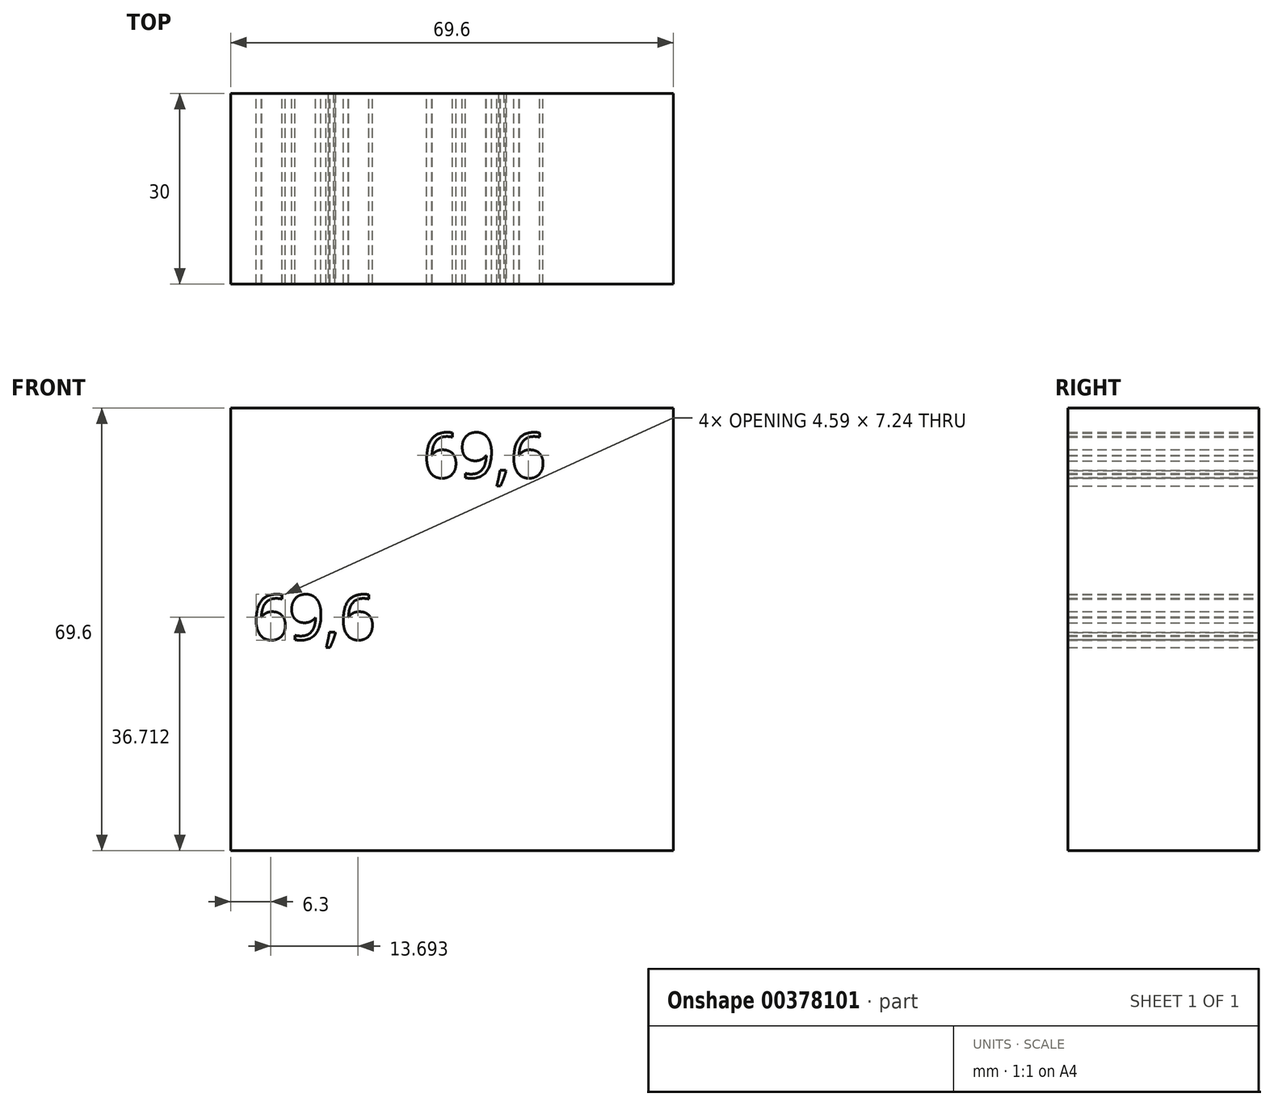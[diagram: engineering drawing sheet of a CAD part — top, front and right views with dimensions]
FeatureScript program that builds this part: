
annotation { "Feature Type Name" : "Feature", "Feature Type Description" : "" }
export const myFeature = defineFeature(function(context is Context, id is Id, definition is map)
    precondition{}
    {
        {
            var Q0;
            Q0=qCreatedBy(makeId("Front.planeOp"),FACE);
            var sketch = newSketch(context, id + "F0", { "sketchPlane" : qUnion([Q0])});
            skLineSegment(sketch, "E0.bottom", {"start": v(-49.76, 29.3) * mm, "end": v(19.84, 29.3) * mm});
            skLineSegment(sketch, "E0.top", {"start": v(-49.76, -40.3) * mm, "end": v(19.84, -40.3) * mm});
            skLineSegment(sketch, "E0.left", {"start": v(-49.76, 29.3) * mm, "end": v(-49.76, -40.3) * mm});
            skLineSegment(sketch, "E0.right", {"start": v(19.84, 29.3) * mm, "end": v(19.84, -40.3) * mm});
            skText(sketch, "E1", { "text": "69,6\n", "fontName": "OpenSans-Regular.ttf"});
            skText(sketch, "E2", { "text": "69,6\n", "fontName": "OpenSans-Regular.ttf"});
            const initialGuessF0  = {"E1": [-0.0195, 0.01836, 1, 0, 0.0071], "E2": [-0.04632, -0.0071, 1, 0, 0.0071]};
            skSetInitialGuess(sketch, initialGuessF0);
            skSolve(sketch);
        }
        {
            var Q0;
            Q0 = qSketchRegion(id + "F0", true);
            extrude(context, id + "F1", {"entities" : qUnion([Q0]), "depth" : 30 * mm});
        }
    });
